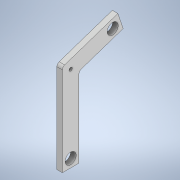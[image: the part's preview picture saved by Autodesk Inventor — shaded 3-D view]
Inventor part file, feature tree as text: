
AUTODESK INVENTOR PART (.ipt)
format: ipt  version: 2020 (Build 240168000, 168)  size: 118,272 bytes
history: native  units: in
note: dims shown in document units (in); Inventor stores cm internally (conversion verified against a paired STEP export)
features: extrude x1, sketch x1
ambient origin geometry x8: Origin, YZ Plane, XZ Plane, XY Plane, X Axis, Y Axis, Z Axis, Center Point
bodies: Solid1 (feature_tree)
feature tree (2):
  extrude  "Extrusion1"  Depth=0.3937in
  sketch  "Sketch1"  dims[d0=0.2362in d1=6.6929in d2=1.1811in d3=4.3307in d6=0.7464in d7=0.5906in d8=0.5906in d9=0.2362in d10=0.7874in d11=0.2362in d12=0.5906in d13=0.7874in d14=0.3937in d15=0.0in]
